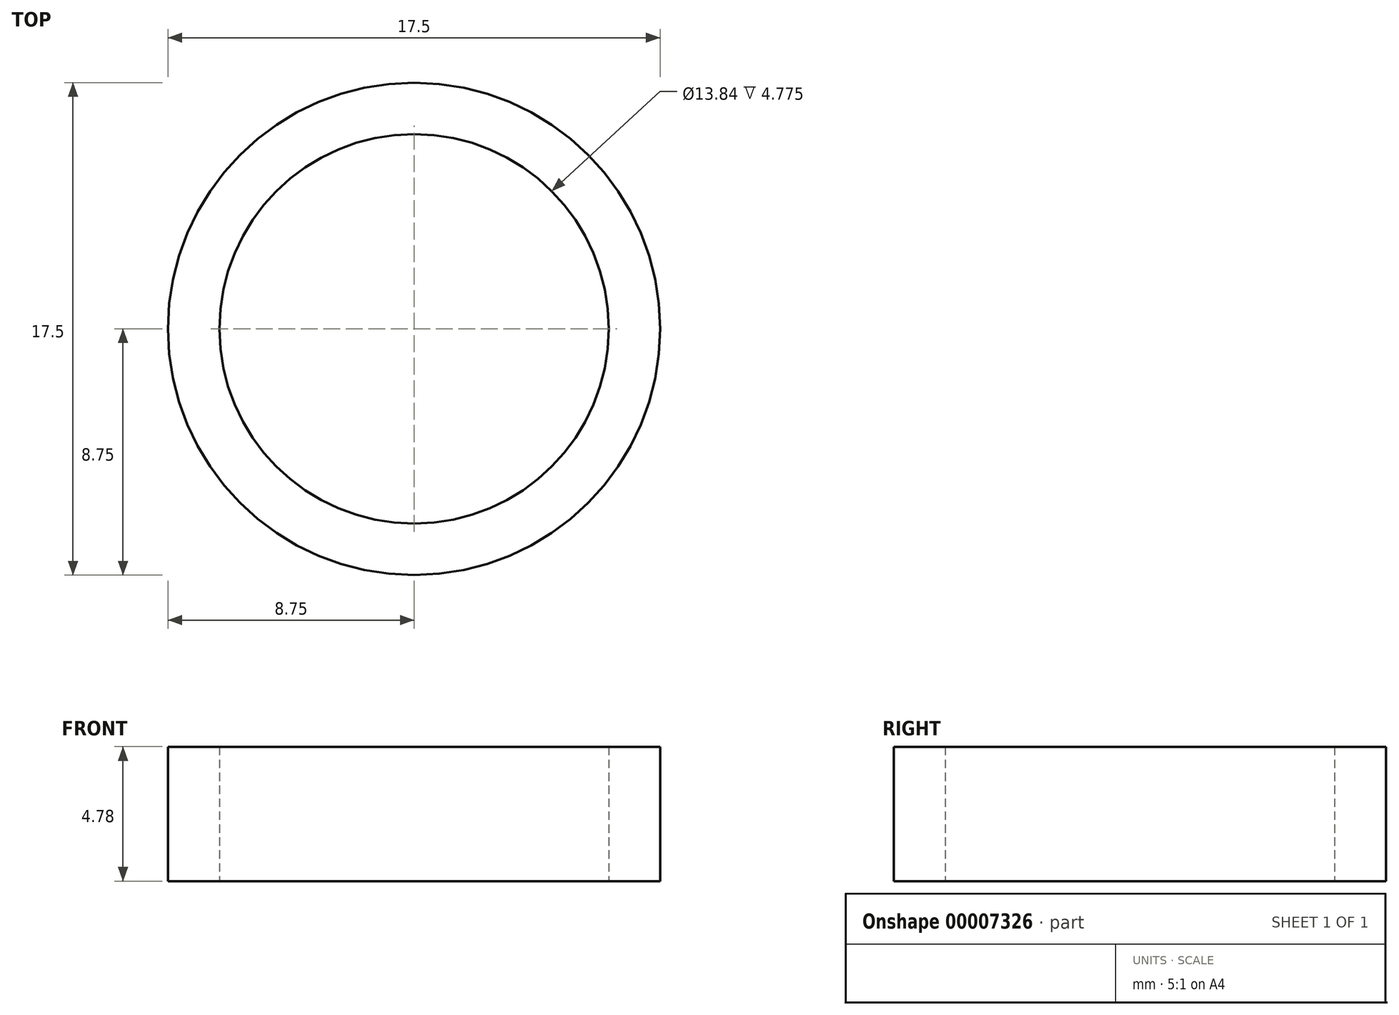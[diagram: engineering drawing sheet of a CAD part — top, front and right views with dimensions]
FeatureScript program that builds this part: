
annotation { "Feature Type Name" : "Feature", "Feature Type Description" : "" }
export const myFeature = defineFeature(function(context is Context, id is Id, definition is map)
    precondition{}
    {
        {
            var Q0;
            Q0=qCreatedBy(makeId("Front.planeOp"),FACE);
            var sketch = newSketch(context, id + "F0", { "sketchPlane" : qUnion([Q0])});
            skLineSegment(sketch, "E0.bottom", {"start": v(6.92, 0) * mm, "end": v(8.75, 0) * mm});
            skLineSegment(sketch, "E0.top", {"start": v(6.92, 4.78) * mm, "end": v(8.75, 4.78) * mm});
            skLineSegment(sketch, "E0.left", {"start": v(6.92, 0) * mm, "end": v(6.92, 4.78) * mm});
            skLineSegment(sketch, "E0.right", {"start": v(8.75, 0) * mm, "end": v(8.75, 4.78) * mm});
            skLineSegment(sketch, "E1", {"start": v(6.92, 0) * mm, "end": v(0, 0) * mm});
            skLineSegment(sketch, "E2", {"start": v(0, 0) * mm, "end": v(0, 4.78) * mm});
            skSolve(sketch);
        }
        {
            var Q0;
            Q0 = qSketchRegion(id + "F0", true);
            var Q1;
            Q1=sQuery(id+"F0.wireOp",EDGE,"E2");
            revolve(context, id + "F1", {"entities" : qUnion([Q0]), "axis" : qUnion([Q1]), "revolveType" : RevolveType.FULL});
        }
    });
